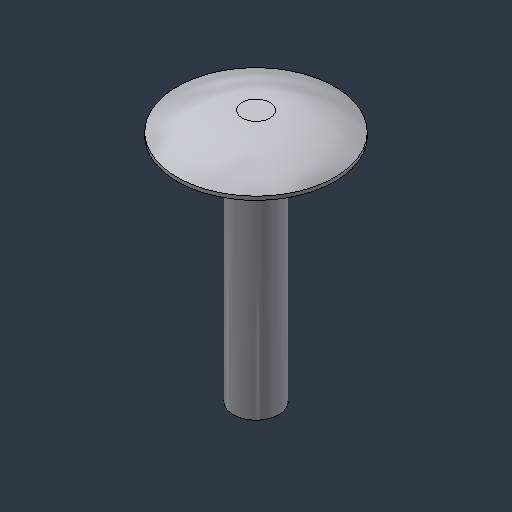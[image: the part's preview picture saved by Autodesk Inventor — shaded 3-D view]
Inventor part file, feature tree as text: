
AUTODESK INVENTOR PART (.ipt)
format: ipt  version: 2024.3 (Build 283343000, 343)  size: 101,888 bytes
history: native  units: mm (DEFAULTED — no unit token found)
features: revolve x1
ambient origin geometry x8: Origin, YZ Plane, XZ Plane, XY Plane, X Axis, Y Axis, Z Axis, Center Point
bodies: Solid1 (feature_tree)
feature tree (1):
  revolve  "Revolve1"  [1 undecoded]
note: 1 required parameter value undecoded (feature->parameter linkage not recoverable at this tier; creation-order binding heuristic only, values carry confidence <= 0.55)
